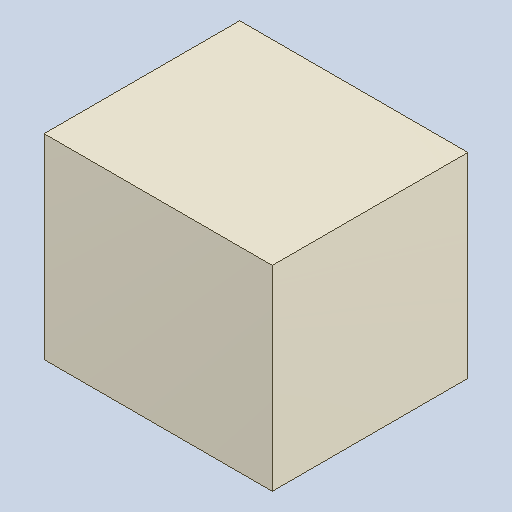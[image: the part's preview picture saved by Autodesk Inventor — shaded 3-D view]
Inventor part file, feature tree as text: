
AUTODESK INVENTOR PART (.ipt)
format: ipt  version: 2023.4 (Build 274418000, 418)  size: 82,432 bytes
history: native  units: mm
features: extrude x1
ambient origin geometry x8: Origin, YZ Plane, XZ Plane, XY Plane, X Axis, Y Axis, Z Axis, Center Point
bodies: Solid1 (feature_tree)
feature tree (1):
  extrude  "Extruded_11"  [1 undecoded]
note: 1 required parameter value undecoded (feature->parameter linkage not recoverable at this tier; creation-order binding heuristic only, values carry confidence <= 0.55)
